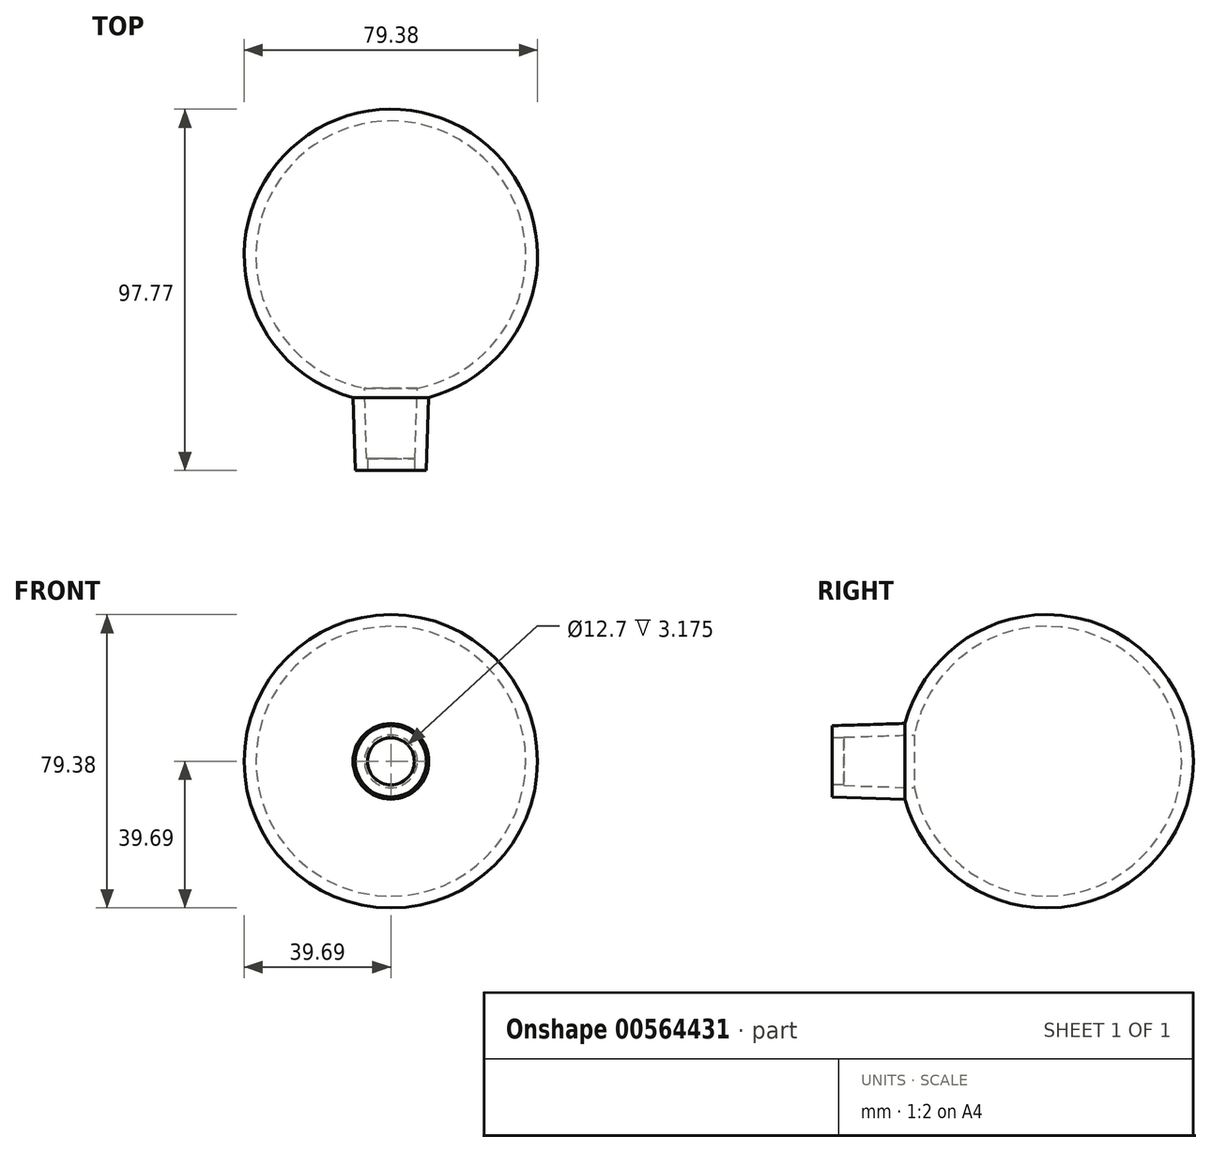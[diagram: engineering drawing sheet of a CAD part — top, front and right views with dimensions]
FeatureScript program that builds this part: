
annotation { "Feature Type Name" : "Feature", "Feature Type Description" : "" }
export const myFeature = defineFeature(function(context is Context, id is Id, definition is map)
    precondition{}
    {
        {
            var Q0;
            Q0=qCreatedBy(makeId("Front.planeOp"),FACE);
            var sketch = newSketch(context, id + "F0", { "sketchPlane" : qUnion([Q0])});
            skArc(sketch, "E0", {"start": v(0, 39.69) * mm, "mid": v(-39.69, 0) * mm, "end": v(0, -39.69) * mm});
            skLineSegment(sketch, "E1", {"start": v(0, 0) * mm, "end": v(0, 39.69) * mm});
            skLineSegment(sketch, "E2", {"start": v(0, 0) * mm, "end": v(0, -39.69) * mm});
            skSolve(sketch);
        }
        {
            var Q0;
            Q0 = qSketchRegion(id + "F0", true);
            var Q1;
            Q1=sQuery(id+"F0.wireOp",EDGE,"E1");
            revolve(context, id + "F1", {"entities" : qUnion([Q0]), "axis" : qUnion([Q1]), "revolveType" : RevolveType.FULL});
        }
        {
            var Q0;
            Q0=qCreatedBy(makeId("Front.planeOp"),FACE);
            cPlane(context, id + "F2", {"entities" : qUnion([Q0]), "cplaneType" : CPlaneType.OFFSET, "offset" : 58.08 * mm, "width" : 152.4 * mm, "height" : 152.4 * mm});
        }
        {
            var Q0;
            Q0=qCreatedBy(id+"F2.planeOp",FACE);
            var sketch = newSketch(context, id + "F3", { "sketchPlane" : qUnion([Q0])});
            skCircle(sketch, "E3", {"center": v(0, 0) * mm, "radius": 9.63 * mm});
            skSolve(sketch);
        }
        {
            var Q0;
            Q0 = qSketchRegion(id + "F3", true);
            var Q1;
            Q1=makeQuery(id+"F1.opRevolve","SWEPT_FACE",FACE,{"disambiguationData":[OSD([sQuery(id+"F0.wireOp",EDGE,"E0")])]});
            extrude(context, id + "F4", {"entities" : qUnion([Q0]), "operationType" : NewBodyOperationType.ADD, "endBound" : BoundingType.UP_TO_SURFACE, "oppositeDirection" : true, "depth" : 25.4 * mm, "endBoundEntityFace" : qUnion([Q1]), "offsetDistance" : 25.4 * mm, "hasDraft" : true, "draftAngle" : 1.78 * degree});
        }
        {
            var Q0;
            Q0=makeQuery(id+"F4.boolean.opBoolean","SPLIT",FACE,{"disambiguationData":[TD([makeQuery(id+"F4.opExtrude","SWEPT_FACE",FACE,{"disambiguationData":[OSD([sQuery(id+"F3.wireOp",EDGE,"pufAI1PE-nQPa-DVg3-p30a-FnrDZTV3sdKf")])]})])],"derivedFrom":makeQuery(id+"F1.opRevolve","SWEPT_FACE",FACE,{"disambiguationData":[OSD([sQuery(id+"F0.wireOp",EDGE,"E0")])]})});
            var Q1;
            Q1=makeQuery(id+"F1.opRevolve","SWEPT_BODY",BODY,{"disambiguationData":[OSD([sQuery(id+"F0.wireOp",EDGE,"E0"),sQuery(id+"F0.wireOp",EDGE,"E1"),sQuery(id+"F0.wireOp",EDGE,"E2")])]});
            shell(context, id + "F5", {"isHollow" : true, "entities" : qUnion([Q0]), "parts" : qUnion([Q1]), "thickness" : 3.17 * mm});
        }
        {
            var Q0;
            Q0=qCreatedBy(id+"F2.planeOp",FACE);
            var sketch = newSketch(context, id + "F6", { "sketchPlane" : qUnion([Q0])});
            skCircle(sketch, "E4", {"center": v(0, 0) * mm, "radius": 6.35 * mm});
            skSolve(sketch);
        }
        {
            var Q0;
            Q0 = qSketchRegion(id + "F6", true);
            extrude(context, id + "F7", {"entities" : qUnion([Q0]), "operationType" : NewBodyOperationType.REMOVE, "oppositeDirection" : true, "depth" : 50.8 * mm, "offsetDistance" : 25.4 * mm});
        }
    });
